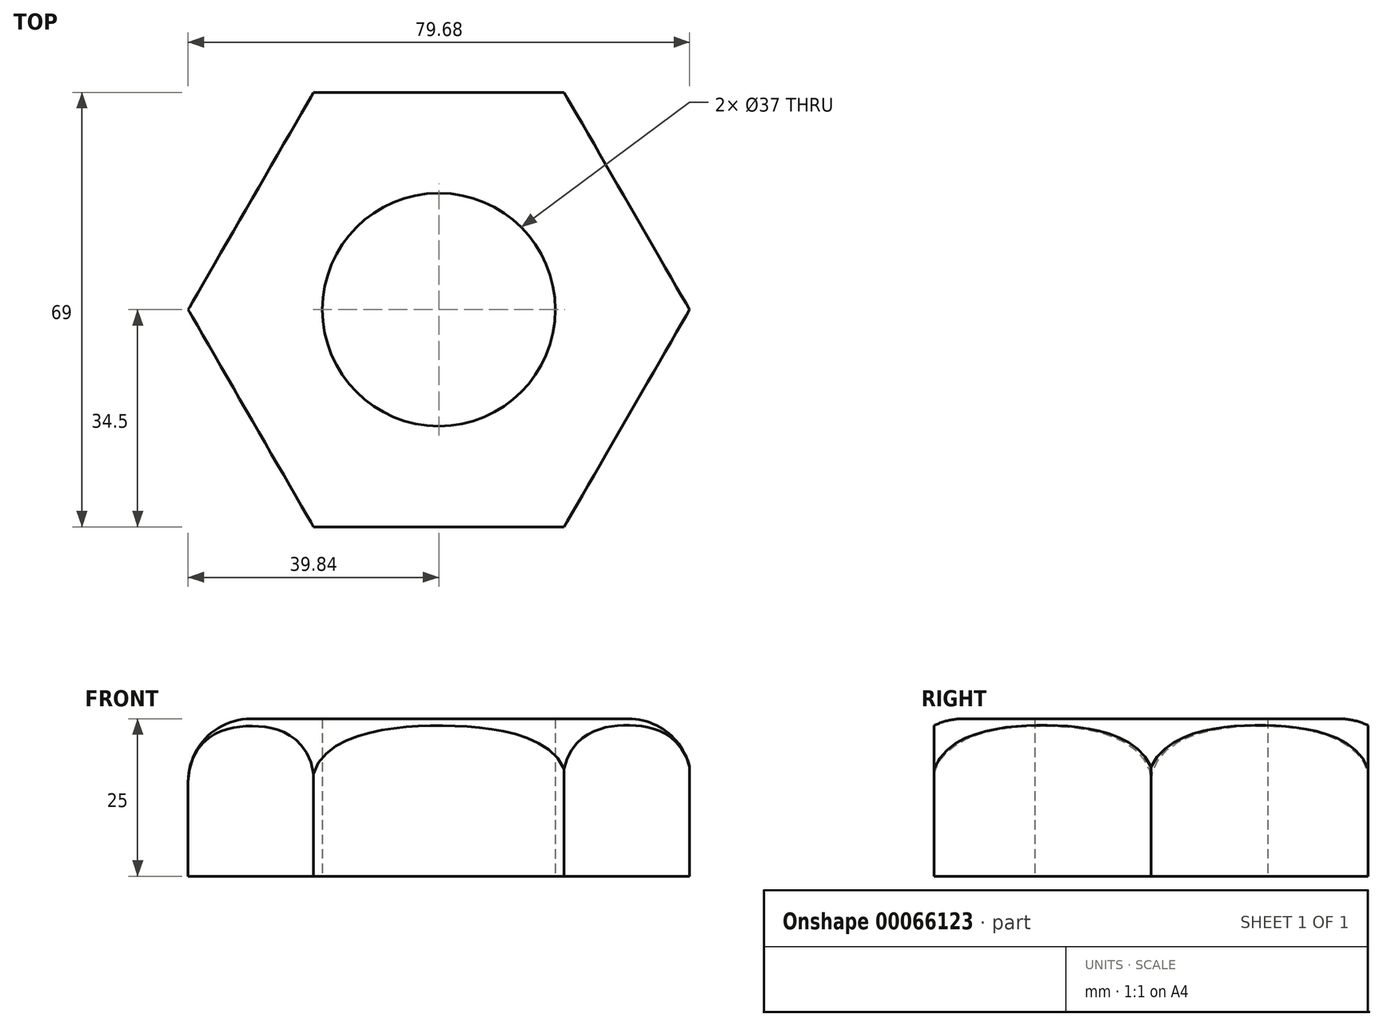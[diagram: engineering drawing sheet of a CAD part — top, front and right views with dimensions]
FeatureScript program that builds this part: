
annotation { "Feature Type Name" : "Feature", "Feature Type Description" : "" }
export const myFeature = defineFeature(function(context is Context, id is Id, definition is map)
    precondition{}
    {
        {
            var Q0;
            Q0=qCreatedBy(makeId("Top.planeOp"),FACE);
            var sketch = newSketch(context, id + "F0", { "sketchPlane" : qUnion([Q0])});
            skCircle(sketch, "E0.cCircle", {"center": v(0, 0) * mm, "radius": 34.5 * mm, "construction": true});
            skLineSegment(sketch, "E0.0", {"start": v(-19.92, 34.5) * mm, "end": v(19.92, 34.5) * mm});
            skLineSegment(sketch, "E0.1", {"start": v(19.92, 34.5) * mm, "end": v(39.84, 0) * mm});
            skLineSegment(sketch, "E0.2", {"start": v(39.84, 0) * mm, "end": v(19.92, -34.5) * mm});
            skLineSegment(sketch, "E0.3", {"start": v(19.92, -34.5) * mm, "end": v(-19.92, -34.5) * mm});
            skLineSegment(sketch, "E0.4", {"start": v(-19.92, -34.5) * mm, "end": v(-39.84, 0) * mm});
            skLineSegment(sketch, "E0.5", {"start": v(-39.84, 0) * mm, "end": v(-19.92, 34.5) * mm});
            skPoint(sketch, "E0.0.midPoint", {"position": v(0, 34.5) * mm});
            skCircle(sketch, "E1", {"center": v(0, 0) * mm, "radius": 18.5 * mm});
            skSolve(sketch);
        }
        {
            var Q0;
            Q0=makeQuery(id+"F0.imprint","IMPRINT",FACE,{"disambiguationData":[TD([[makeQuery(id+"F0.imprint","IMPRINT",EDGE,{"derivedFrom":sQuery(id+"F0.wireOp",EDGE,"E0.0")}),-1.0]])]});
            extrude(context, id + "F1", {"entities" : qUnion([Q0]), "depth" : 25 * mm});
        }
        {
            var Q0;
            Q0=qCreatedBy(makeId("Front.planeOp"),FACE);
            var sketch = newSketch(context, id + "F2", { "sketchPlane" : qUnion([Q0])});
            skLineSegment(sketch, "E2", {"start": v(-39.84, 0) * mm, "end": v(-39.84, 15) * mm});
            skLineSegment(sketch, "E3", {"start": v(-29.84, 25) * mm, "end": v(0.15, 25) * mm});
            skLineSegment(sketch, "E4", {"start": v(0.15, 25) * mm, "end": v(0.15, 38.47) * mm});
            skLineSegment(sketch, "E5", {"start": v(0.15, 38.47) * mm, "end": v(-48.75, 38.47) * mm});
            skLineSegment(sketch, "E6", {"start": v(-48.75, 38.47) * mm, "end": v(-48.75, 0) * mm});
            skLineSegment(sketch, "E7", {"start": v(-48.75, 0) * mm, "end": v(-39.84, 0) * mm});
            skPoint(sketch, "E8.visualSharp", {"position": v(-39.84, 25) * mm});
            skArc(sketch, "E8.filletArc", {"start": v(-29.84, 25) * mm, "mid": v(-36.9, 22.07) * mm, "end": v(-39.84, 15) * mm});
            skSolve(sketch);
        }
        {
            var Q0;
            Q0=makeQuery(id+"F2.imprint","IMPRINT",FACE,{"disambiguationData":[TD([[makeQuery(id+"F2.imprint","IMPRINT",EDGE,{"derivedFrom":sQuery(id+"F2.wireOp",EDGE,"E2")}),1.0]])]});
            var Q1;
            Q1=sQuery(id+"F2.wireOp",EDGE,"E4");
            revolve(context, id + "F3", {"operationType" : NewBodyOperationType.REMOVE, "entities" : qUnion([Q0]), "axis" : qUnion([Q1]), "revolveType" : RevolveType.FULL, "oppositeDirection" : true});
        }
    });
